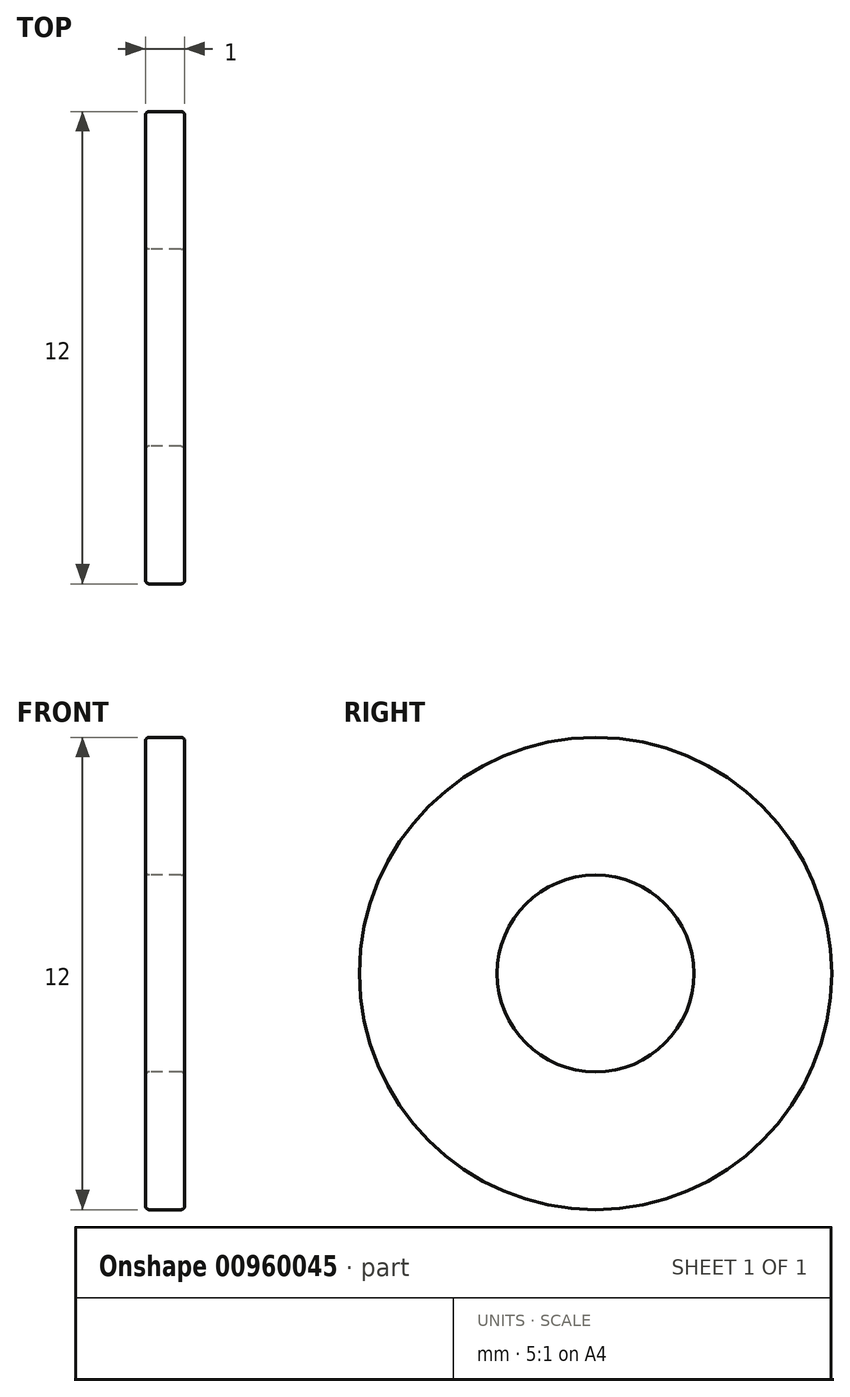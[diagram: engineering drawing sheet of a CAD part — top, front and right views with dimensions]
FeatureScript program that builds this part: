
annotation { "Feature Type Name" : "Feature", "Feature Type Description" : "" }
export const myFeature = defineFeature(function(context is Context, id is Id, definition is map)
    precondition{}
    {
        {
            var Q0;
            Q0=qCreatedBy(makeId("Right.planeOp"),FACE);
            var sketch = newSketch(context, id + "F0", { "sketchPlane" : qUnion([Q0])});
            skCircle(sketch, "E0", {"center": v(0, 0) * mm, "radius": 2.5 * mm});
            skCircle(sketch, "E1", {"center": v(0, 0) * mm, "radius": 6 * mm});
            skSolve(sketch);
        }
        {
            var Q0;
            Q0 = qSketchRegion(id + "F0", true);
            extrude(context, id + "F1", {"entities" : qUnion([Q0]), "depth" : 1 * mm, "offsetDistance" : 25 * mm});
        }
        {
            var Q0;
            Q0=makeQuery(id+"F1.opExtrude","CAP_EDGE",EDGE,{"disambiguationData":[OSD([sQuery(id+"F0.wireOp",EDGE,"E1")])],"isStart":false});
            var Q1;
            Q1=makeQuery(id+"F1.opExtrude","CAP_EDGE",EDGE,{"disambiguationData":[OSD([sQuery(id+"F0.wireOp",EDGE,"E1")])],"isStart":true});
            fillet(context, id + "F2", {"entities" : qUnion([Q0, Q1]), "radius" : 0.1 * mm, "tangentPropagation" : true, "allowEdgeOverflow" : false});
        }
        {
            var Q0;
            Q0=makeQuery(id+"F1.opExtrude","CAP_EDGE",EDGE,{"disambiguationData":[OSD([sQuery(id+"F0.wireOp",EDGE,"E0")])],"isStart":true});
            var Q1;
            Q1=makeQuery(id+"F1.opExtrude","CAP_EDGE",EDGE,{"disambiguationData":[OSD([sQuery(id+"F0.wireOp",EDGE,"E0")])],"isStart":false});
            fillet(context, id + "F3", {"entities" : qUnion([Q0, Q1]), "radius" : 0.1 * mm, "tangentPropagation" : true, "allowEdgeOverflow" : false});
        }
    });
